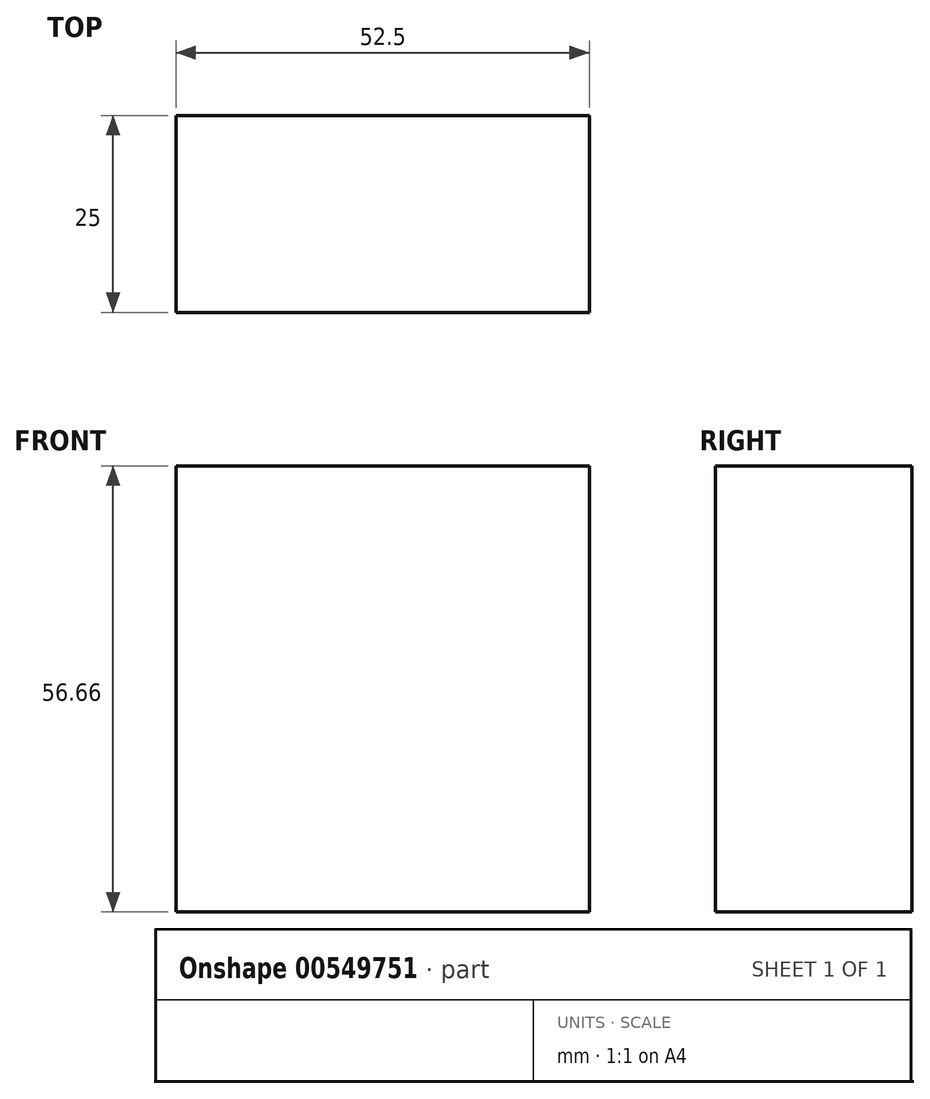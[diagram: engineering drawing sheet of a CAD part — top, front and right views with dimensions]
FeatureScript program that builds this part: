
annotation { "Feature Type Name" : "Feature", "Feature Type Description" : "" }
export const myFeature = defineFeature(function(context is Context, id is Id, definition is map)
    precondition{}
    {
        {
            var Q0;
            Q0=qCreatedBy(makeId("Front.planeOp"),FACE);
            var sketch = newSketch(context, id + "F0", { "sketchPlane" : qUnion([Q0])});
            skLineSegment(sketch, "E0.bottom", {"start": v(-26.82, 29.65) * mm, "end": v(25.68, 29.65) * mm});
            skLineSegment(sketch, "E0.top", {"start": v(-26.82, -27) * mm, "end": v(25.68, -27) * mm});
            skLineSegment(sketch, "E0.left", {"start": v(-26.82, 29.65) * mm, "end": v(-26.82, -27) * mm});
            skLineSegment(sketch, "E0.right", {"start": v(25.68, 29.65) * mm, "end": v(25.68, -27) * mm});
            skSolve(sketch);
        }
        {
            var Q0;
            Q0 = qSketchRegion(id + "F0", true);
            extrude(context, id + "F1", {"entities" : qUnion([Q0]), "depth" : 25 * mm, "offsetDistance" : 25 * mm});
        }
    });
